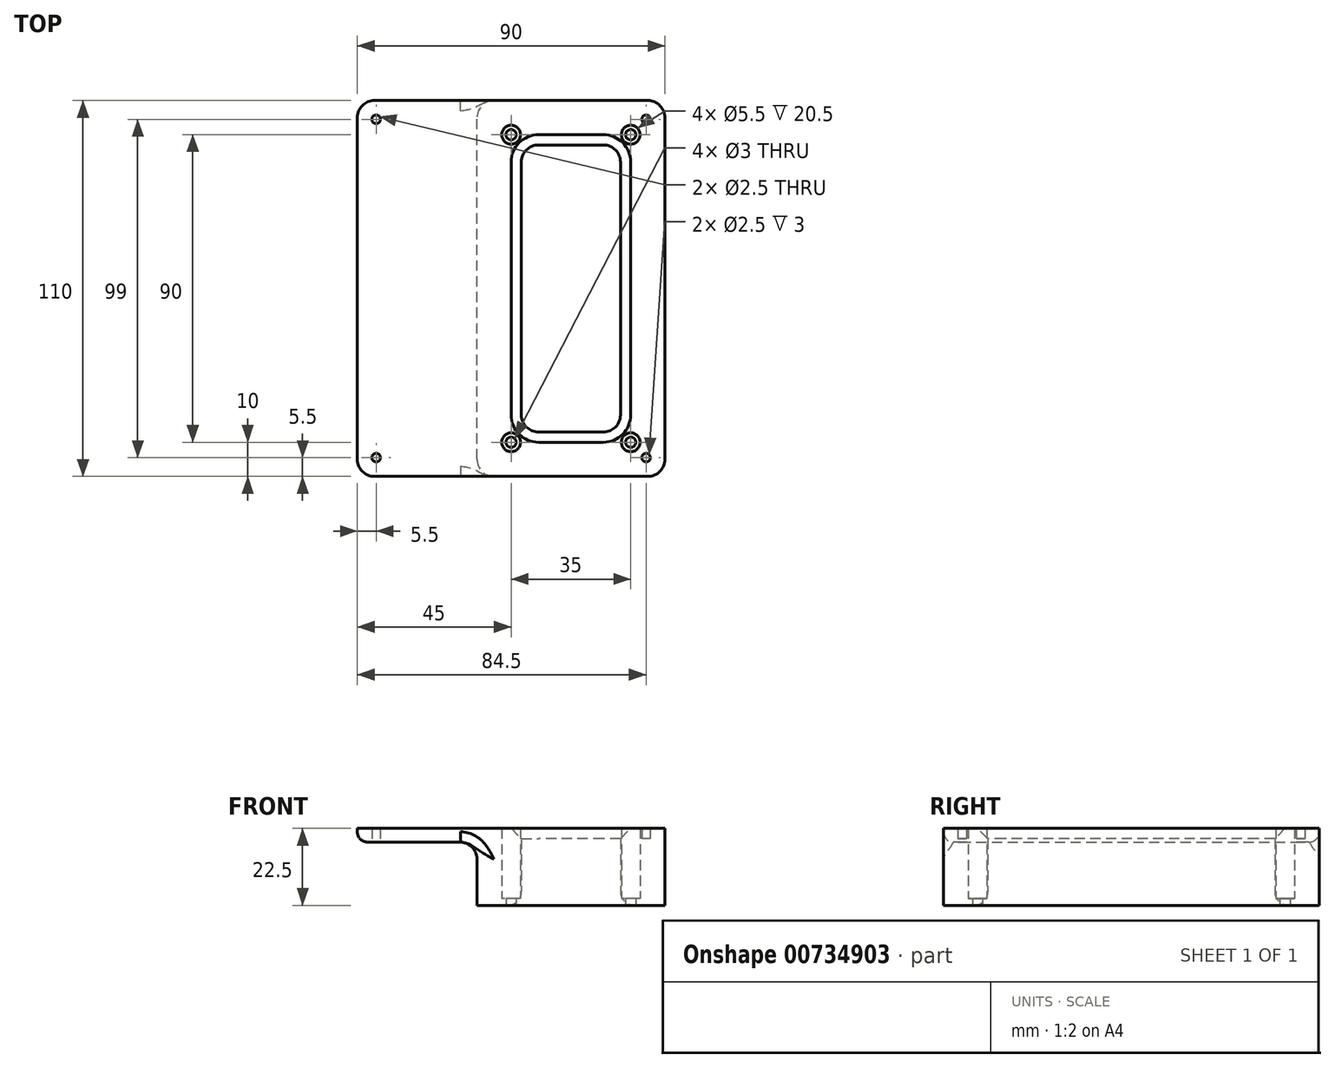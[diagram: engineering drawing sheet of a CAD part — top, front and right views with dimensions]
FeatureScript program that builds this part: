
annotation { "Feature Type Name" : "Feature", "Feature Type Description" : "" }
export const myFeature = defineFeature(function(context is Context, id is Id, definition is map)
    precondition{}
    {
        {
            var Q0;
            Q0=qCreatedBy(makeId("Top.planeOp"),FACE);
            var sketch = newSketch(context, id + "F0", { "sketchPlane" : qUnion([Q0])});
            skLineSegment(sketch, "E0.bottom", {"start": v(-5, 0) * mm, "end": v(-50, 0) * mm});
            skLineSegment(sketch, "E0.top", {"start": v(-5, 110) * mm, "end": v(-50, 110) * mm});
            skLineSegment(sketch, "E0.left", {"start": v(0, 5) * mm, "end": v(0, 105) * mm});
            skLineSegment(sketch, "E0.right", {"start": v(-55, 5) * mm, "end": v(-55, 105) * mm});
            skPoint(sketch, "E1.visualSharp", {"position": v(-55, 110) * mm});
            skArc(sketch, "E1.filletArc", {"start": v(-50, 110) * mm, "mid": v(-53.54, 108.54) * mm, "end": v(-55, 105) * mm});
            skPoint(sketch, "E2.visualSharp", {"position": v(0, 110) * mm});
            skArc(sketch, "E2.filletArc", {"start": v(0, 105) * mm, "mid": v(-1.46, 108.54) * mm, "end": v(-5, 110) * mm});
            skPoint(sketch, "E3.visualSharp", {"position": v(0, 0) * mm});
            skArc(sketch, "E3.filletArc", {"start": v(-5, 0) * mm, "mid": v(-1.46, 1.46) * mm, "end": v(0, 5) * mm});
            skPoint(sketch, "E4.visualSharp", {"position": v(-55, 0) * mm});
            skArc(sketch, "E4.filletArc", {"start": v(-55, 5) * mm, "mid": v(-53.54, 1.46) * mm, "end": v(-50, 0) * mm});
            skCircle(sketch, "E5", {"center": v(-10, 100) * mm, "radius": 1.5 * mm});
            skCircle(sketch, "E6", {"center": v(-10, 10) * mm, "radius": 1.5 * mm});
            skCircle(sketch, "E7", {"center": v(-45, 100) * mm, "radius": 1.5 * mm});
            skCircle(sketch, "E8.0", {"center": v(-45, 100) * mm, "radius": 2.75 * mm});
            skCircle(sketch, "E9.0", {"center": v(-10, 100) * mm, "radius": 2.75 * mm});
            skCircle(sketch, "E10", {"center": v(-45, 10) * mm, "radius": 1.5 * mm});
            skCircle(sketch, "E11.0", {"center": v(-45, 10) * mm, "radius": 2.75 * mm});
            skCircle(sketch, "E12.0", {"center": v(-10, 10) * mm, "radius": 2.75 * mm});
            skLineSegment(sketch, "E13.bottom", {"start": v(-37, 97) * mm, "end": v(-18, 97) * mm});
            skLineSegment(sketch, "E13.top", {"start": v(-37, 13) * mm, "end": v(-18, 13) * mm});
            skLineSegment(sketch, "E13.left", {"start": v(-42, 92) * mm, "end": v(-42, 18) * mm});
            skLineSegment(sketch, "E13.right", {"start": v(-13, 92) * mm, "end": v(-13, 18) * mm});
            skPoint(sketch, "E14.visualSharp", {"position": v(-42, 13) * mm});
            skArc(sketch, "E14.filletArc", {"start": v(-42, 18) * mm, "mid": v(-40.54, 14.46) * mm, "end": v(-37, 13) * mm});
            skPoint(sketch, "E15.visualSharp", {"position": v(-13, 13) * mm});
            skArc(sketch, "E15.filletArc", {"start": v(-18, 13) * mm, "mid": v(-14.46, 14.46) * mm, "end": v(-13, 18) * mm});
            skPoint(sketch, "E16.visualSharp", {"position": v(-42, 97) * mm});
            skArc(sketch, "E16.filletArc", {"start": v(-37, 97) * mm, "mid": v(-40.54, 95.54) * mm, "end": v(-42, 92) * mm});
            skPoint(sketch, "E17.visualSharp", {"position": v(-13, 97) * mm});
            skArc(sketch, "E17.filletArc", {"start": v(-13, 92) * mm, "mid": v(-14.46, 95.54) * mm, "end": v(-18, 97) * mm});
            skSolve(sketch);
        }
        {
            var Q0;
            Q0 = qSketchRegion(id + "F0", true);
            extrude(context, id + "F1", {"entities" : qUnion([Q0]), "depth" : 19.5 * mm, "offsetDistance" : 25 * mm});
        }
        {
            var Q0;
            Q0=makeQuery(id+"F0.imprint","IMPRINT",FACE,{"disambiguationData":[TD([[makeQuery(id+"F0.imprint","IMPRINT",EDGE,{"derivedFrom":sQuery(id+"F0.wireOp",EDGE,"E10")}),-1.0]])]});
            var Q1;
            Q1=makeQuery(id+"F0.imprint","IMPRINT",FACE,{"disambiguationData":[TD([[makeQuery(id+"F0.imprint","IMPRINT",EDGE,{"derivedFrom":sQuery(id+"F0.wireOp",EDGE,"E6")}),-1.0]])]});
            var Q2;
            Q2=makeQuery(id+"F0.imprint","IMPRINT",FACE,{"disambiguationData":[TD([[makeQuery(id+"F0.imprint","IMPRINT",EDGE,{"derivedFrom":sQuery(id+"F0.wireOp",EDGE,"E7")}),-1.0]])]});
            var Q3;
            Q3=makeQuery(id+"F0.imprint","IMPRINT",FACE,{"disambiguationData":[TD([[makeQuery(id+"F0.imprint","IMPRINT",EDGE,{"derivedFrom":sQuery(id+"F0.wireOp",EDGE,"E5")}),-1.0]])]});
            extrude(context, id + "F2", {"entities" : qUnion([Q0, Q1, Q2, Q3]), "operationType" : NewBodyOperationType.ADD, "depth" : 2 * mm, "offsetDistance" : 25 * mm});
        }
        {
            var Q0;
            Q0=makeQuery(id+"F1.opExtrude","CAP_FACE",FACE,{"disambiguationData":[OSD([sQuery(id+"F0.wireOp",EDGE,"E0.bottom"),sQuery(id+"F0.wireOp",EDGE,"E0.top"),sQuery(id+"F0.wireOp",EDGE,"E0.left"),sQuery(id+"F0.wireOp",EDGE,"E0.right"),sQuery(id+"F0.wireOp",EDGE,"E1.filletArc"),sQuery(id+"F0.wireOp",EDGE,"E2.filletArc"),sQuery(id+"F0.wireOp",EDGE,"E3.filletArc"),sQuery(id+"F0.wireOp",EDGE,"E4.filletArc"),sQuery(id+"F0.wireOp",EDGE,"E8.0"),sQuery(id+"F0.wireOp",EDGE,"E9.0"),sQuery(id+"F0.wireOp",EDGE,"E11.0"),sQuery(id+"F0.wireOp",EDGE,"E12.0")])],"isStart":false});
            var sketch = newSketch(context, id + "F3", { "sketchPlane" : qUnion([Q0])});
            skLineSegment(sketch, "E18.bottom", {"start": v(-5, 0) * mm, "end": v(-85, 0) * mm});
            skLineSegment(sketch, "E18.top", {"start": v(-5, 110) * mm, "end": v(-85, 110) * mm});
            skLineSegment(sketch, "E18.left", {"start": v(0, 5) * mm, "end": v(0, 105) * mm});
            skLineSegment(sketch, "E18.right", {"start": v(-90, 5) * mm, "end": v(-90, 105) * mm});
            skPoint(sketch, "E19.visualSharp", {"position": v(-90, 110) * mm});
            skArc(sketch, "E19.filletArc", {"start": v(-85, 110) * mm, "mid": v(-88.54, 108.54) * mm, "end": v(-90, 105) * mm});
            skPoint(sketch, "E20.visualSharp", {"position": v(0, 110) * mm});
            skArc(sketch, "E20.filletArc", {"start": v(0, 105) * mm, "mid": v(-1.46, 108.54) * mm, "end": v(-5, 110) * mm});
            skPoint(sketch, "E21.visualSharp", {"position": v(0, 0) * mm});
            skArc(sketch, "E21.filletArc", {"start": v(-5, 0) * mm, "mid": v(-1.46, 1.46) * mm, "end": v(0, 5) * mm});
            skPoint(sketch, "E22.visualSharp", {"position": v(-90, 0) * mm});
            skArc(sketch, "E22.filletArc", {"start": v(-90, 5) * mm, "mid": v(-88.54, 1.46) * mm, "end": v(-85, 0) * mm});
            skCircle(sketch, "E23.0", {"center": v(-45, 100) * mm, "radius": 2.75 * mm});
            skCircle(sketch, "E24.0", {"center": v(-10, 100) * mm, "radius": 2.75 * mm});
            skCircle(sketch, "E25.0", {"center": v(-45, 10) * mm, "radius": 2.75 * mm});
            skCircle(sketch, "E26.0", {"center": v(-10, 10) * mm, "radius": 2.75 * mm});
            skCircle(sketch, "E27", {"center": v(-84.5, 104.5) * mm, "radius": 1.25 * mm});
            skCircle(sketch, "E28", {"center": v(-5.5, 104.5) * mm, "radius": 1.25 * mm});
            skCircle(sketch, "E29", {"center": v(-5.5, 5.5) * mm, "radius": 1.25 * mm});
            skCircle(sketch, "E30", {"center": v(-84.5, 5.5) * mm, "radius": 1.25 * mm});
            skSolve(sketch);
        }
        {
            var Q0;
            Q0 = qSketchRegion(id + "F3", true);
            extrude(context, id + "F4", {"entities" : qUnion([Q0]), "operationType" : NewBodyOperationType.ADD, "depth" : 3 * mm, "offsetDistance" : 25 * mm});
        }
        {
            var Q0;
            Q0 = qSketchRegion(id + "F3", true);
            extrude(context, id + "F5", {"entities" : qUnion([Q0]), "operationType" : NewBodyOperationType.ADD, "oppositeDirection" : true, "depth" : 1 * mm, "offsetDistance" : 25 * mm});
        }
        {
            var Q0;
            Q0=makeQuery(id+"F5.boolean.opBoolean","INTERSECT",EDGE,{"derivedFrom":[makeQuery(id+"F1.opExtrude","SWEPT_FACE",FACE,{"disambiguationData":[OSD([sQuery(id+"F0.wireOp",EDGE,"E0.right")])]}),makeQuery(id+"F5.opExtrude","CAP_FACE",FACE,{"disambiguationData":[OSD([sQuery(id+"F3.wireOp",EDGE,"E18.bottom"),sQuery(id+"F3.wireOp",EDGE,"E18.top"),sQuery(id+"F3.wireOp",EDGE,"E18.left"),sQuery(id+"F3.wireOp",EDGE,"E18.right"),sQuery(id+"F3.wireOp",EDGE,"E19.filletArc"),sQuery(id+"F3.wireOp",EDGE,"E20.filletArc"),sQuery(id+"F3.wireOp",EDGE,"E21.filletArc"),sQuery(id+"F3.wireOp",EDGE,"E22.filletArc"),sQuery(id+"F3.wireOp",EDGE,"E23.0"),sQuery(id+"F3.wireOp",EDGE,"E24.0"),sQuery(id+"F3.wireOp",EDGE,"E25.0"),sQuery(id+"F3.wireOp",EDGE,"E26.0"),sQuery(id+"F3.wireOp",EDGE,"E27"),sQuery(id+"F3.wireOp",EDGE,"E28"),sQuery(id+"F3.wireOp",EDGE,"E29"),sQuery(id+"F3.wireOp",EDGE,"E30")])],"isStart":false})]});
            var Q1;
            Q1=makeQuery(id+"F5.boolean.opBoolean","INTERSECT",EDGE,{"derivedFrom":[makeQuery(id+"F1.opExtrude","SWEPT_FACE",FACE,{"disambiguationData":[OSD([sQuery(id+"F0.wireOp",EDGE,"E1.filletArc")])]}),makeQuery(id+"F5.opExtrude","CAP_FACE",FACE,{"disambiguationData":[OSD([sQuery(id+"F3.wireOp",EDGE,"E18.bottom"),sQuery(id+"F3.wireOp",EDGE,"E18.top"),sQuery(id+"F3.wireOp",EDGE,"E18.left"),sQuery(id+"F3.wireOp",EDGE,"E18.right"),sQuery(id+"F3.wireOp",EDGE,"E19.filletArc"),sQuery(id+"F3.wireOp",EDGE,"E20.filletArc"),sQuery(id+"F3.wireOp",EDGE,"E21.filletArc"),sQuery(id+"F3.wireOp",EDGE,"E22.filletArc"),sQuery(id+"F3.wireOp",EDGE,"E23.0"),sQuery(id+"F3.wireOp",EDGE,"E24.0"),sQuery(id+"F3.wireOp",EDGE,"E25.0"),sQuery(id+"F3.wireOp",EDGE,"E26.0"),sQuery(id+"F3.wireOp",EDGE,"E27"),sQuery(id+"F3.wireOp",EDGE,"E28"),sQuery(id+"F3.wireOp",EDGE,"E29"),sQuery(id+"F3.wireOp",EDGE,"E30")])],"isStart":false})]});
            var Q2;
            Q2=makeQuery(id+"F5.boolean.opBoolean","INTERSECT",EDGE,{"derivedFrom":[makeQuery(id+"F1.opExtrude","SWEPT_FACE",FACE,{"disambiguationData":[OSD([sQuery(id+"F0.wireOp",EDGE,"E4.filletArc")])]}),makeQuery(id+"F5.opExtrude","CAP_FACE",FACE,{"disambiguationData":[OSD([sQuery(id+"F3.wireOp",EDGE,"E18.bottom"),sQuery(id+"F3.wireOp",EDGE,"E18.top"),sQuery(id+"F3.wireOp",EDGE,"E18.left"),sQuery(id+"F3.wireOp",EDGE,"E18.right"),sQuery(id+"F3.wireOp",EDGE,"E19.filletArc"),sQuery(id+"F3.wireOp",EDGE,"E20.filletArc"),sQuery(id+"F3.wireOp",EDGE,"E21.filletArc"),sQuery(id+"F3.wireOp",EDGE,"E22.filletArc"),sQuery(id+"F3.wireOp",EDGE,"E23.0"),sQuery(id+"F3.wireOp",EDGE,"E24.0"),sQuery(id+"F3.wireOp",EDGE,"E25.0"),sQuery(id+"F3.wireOp",EDGE,"E26.0"),sQuery(id+"F3.wireOp",EDGE,"E27"),sQuery(id+"F3.wireOp",EDGE,"E28"),sQuery(id+"F3.wireOp",EDGE,"E29"),sQuery(id+"F3.wireOp",EDGE,"E30")])],"isStart":false})]});
            fillet(context, id + "F6", {"entities" : qUnion([Q0, Q1, Q2]), "radius" : 5 * mm, "tangentPropagation" : true, "allowEdgeOverflow" : false});
        }
        {
            var Q0;
            Q0=makeQuery(id+"F5.opExtrude","CAP_EDGE",EDGE,{"disambiguationData":[OSD([sQuery(id+"F3.wireOp",EDGE,"E18.top")])],"isStart":false});
            fillet(context, id + "F7", {"entities" : qUnion([Q0]), "radius" : 3 * mm, "tangentPropagation" : true, "allowEdgeOverflow" : false});
        }
        {
            var Q0;
            Q0=makeQuery(id+"F0.imprint","IMPRINT",FACE,{"disambiguationData":[TD([[makeQuery(id+"F0.imprint","IMPRINT",EDGE,{"derivedFrom":sQuery(id+"F0.wireOp",EDGE,"E13.bottom")}),-1.0]])]});
            extrude(context, id + "F8", {"entities" : qUnion([Q0]), "operationType" : NewBodyOperationType.REMOVE, "depth" : 23.5 * mm, "offsetDistance" : 25 * mm});
        }
        {
            var Q0;
            Q0=makeQuery(id+"F8.boolean.opBoolean","INTERSECT",EDGE,{"derivedFrom":[makeQuery(id+"F4.opExtrude","CAP_FACE",FACE,{"disambiguationData":[OSD([sQuery(id+"F3.wireOp",EDGE,"E18.bottom"),sQuery(id+"F3.wireOp",EDGE,"E18.top"),sQuery(id+"F3.wireOp",EDGE,"E18.left"),sQuery(id+"F3.wireOp",EDGE,"E18.right"),sQuery(id+"F3.wireOp",EDGE,"E19.filletArc"),sQuery(id+"F3.wireOp",EDGE,"E20.filletArc"),sQuery(id+"F3.wireOp",EDGE,"E21.filletArc"),sQuery(id+"F3.wireOp",EDGE,"E22.filletArc"),sQuery(id+"F3.wireOp",EDGE,"E23.0"),sQuery(id+"F3.wireOp",EDGE,"E24.0"),sQuery(id+"F3.wireOp",EDGE,"E25.0"),sQuery(id+"F3.wireOp",EDGE,"E26.0"),sQuery(id+"F3.wireOp",EDGE,"E27"),sQuery(id+"F3.wireOp",EDGE,"E28"),sQuery(id+"F3.wireOp",EDGE,"E29"),sQuery(id+"F3.wireOp",EDGE,"E30")])],"isStart":false}),makeQuery(id+"F8.opExtrude","SWEPT_FACE",FACE,{"disambiguationData":[OSD([sQuery(id+"F0.wireOp",EDGE,"E13.left")])]})]});
            chamfer(context, id + "F9", {"entities" : qUnion([Q0]), "width" : 3 * mm, "tangentPropagation" : true});
        }
        {
            var Q0;
            Q0=makeQuery(id+"F1.opExtrude","CAP_EDGE",EDGE,{"disambiguationData":[OSD([sQuery(id+"F0.wireOp",EDGE,"E13.left")])],"isStart":true});
            fillet(context, id + "F10", {"entities" : qUnion([Q0]), "radius" : 4 * mm, "tangentPropagation" : true, "allowEdgeOverflow" : false});
        }
    });
